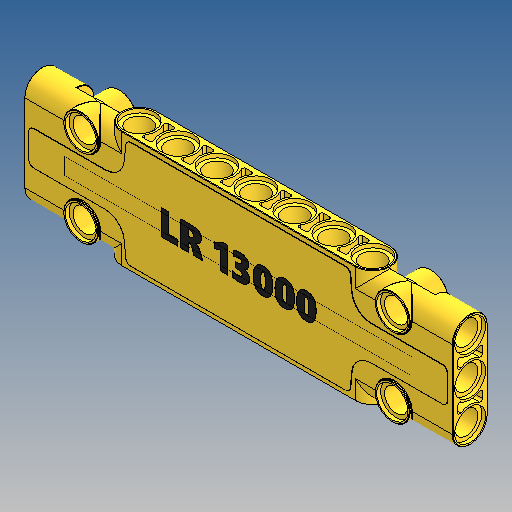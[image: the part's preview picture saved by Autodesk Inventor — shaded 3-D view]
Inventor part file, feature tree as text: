
AUTODESK INVENTOR PART (.ipt)
format: ipt  version: 2025 (Build 290162010, 162A)  size: 1,306,624 bytes
history: native  units: in
note: dims shown in document units (in); Inventor stores cm internally (conversion verified against a paired STEP export)
features: extrude x18, sketch x13, mirror x5, plane x1, fillet x1
ambient origin geometry x8: Origin, YZ Plane, XZ Plane, XY Plane, X Axis, Y Axis, Z Axis, Center Point
bodies: Solid1 (feature_tree)
feature tree (38):
  extrude  "Extrusion1"  Depth=0.189in
  sketch  "Sketch3"  dims[d6=0.189in d7=0.252in]
  extrude  "Extrusion2"  Depth=0.0315in
  extrude  "Extrusion3"  TaperAngle=0.0deg  [1 undecoded]
  extrude  "Extrusion4"  Depth=0.252in
  plane  "Work Plane1"
  extrude  "Extrusion5"  Depth=0.7874in
  sketch  "Sketch5"  dims[d12=0.3937in d14=0.3937in d16=0.2835in]
  extrude  "Extrusion6"  Depth=0.2835in
  extrude  "Extrusion7"  Depth=0.0315in
  extrude  "Extrusion10"  Depth=0.2205in TaperAngle=0.0deg
  extrude  "Extrusion8"  Depth=0.189in
  extrude  "Extrusion9"  Depth=0.0315in TaperAngle=0.0deg
  mirror  "Mirror1"
  mirror  "Mirror2"
  sketch  "Sketch8"  dims[d22=-0.1417in d23=0.189in]
  extrude  "Extrusion11"  Depth=0.189in
  extrude  "Extrusion12"  Depth=0.2677in
  extrude  "Extrusion13"  Depth=0.2677in TaperAngle=0.0deg
  sketch  "Sketch9"  dims[d24=0.2835in d25=0.0315in d26=0.0in]
  extrude  "Extrusion14"  Depth=0.252in
  extrude  "Extrusion16"  Depth=0.0315in
  mirror  "Mirror3"
  extrude  "Extrusion15"  TaperAngle=0.0deg  [1 undecoded]
  fillet  "Fillet1"  Radius=0.252in
  extrude  "Extrusion17"  Depth=0.0315in
  mirror  "Spiegeln4"
  mirror  "Spiegeln5"
  extrude  "Extrusion18"  TaperAngle=0.0deg  [1 undecoded]
  sketch  "Sketch2"  dims[d2=0.2835in d3=0.0315in]
  sketch  "Skizze - Rechteckige Anordnung1"  dims[d0=0.315in d1=0.189in]
  sketch  "Sketch4"  dims[d8=45.0deg d9=0.7874in d11=0.315in]
  sketch  "Sketch6"  dims[d17=0.0in d18=0.0315in]
  sketch  "Sketch7"  dims[d19=0.0in d20=0.2205in d21=0.0in]
  sketch  "Sketch10"  dims[d27=0.2835in d28=0.189in]
  sketch  "Skizze - Rechteckige Anordnung2"  dims[d4=3.4646in d5=0.0in]
  sketch  "Skizze11"  dims[d29=1.2598in d30=0.2677in d31=0.0472in]
  sketch  "Skizze12"  dims[d32=0.0in d33=0.0in d34=0.2677in d35=0.0in d36=0.252in d37=0.0315in d38=0.0in d39=0.252in d40=0.0315in d41=0.0in d42=0.0315in d43=0.2205in d44=0.0in d45=0.2835in d46=1.8898in d47=0.189in d48=0.1417in d49=0.1417in d50=0.0in d51=0.0in d52=0.1417in d53=0.0in d54=0.315in d55=0.0in d56=0.252in d57=0.0315in d58=0.0in d59=2.8031in d60=0.126in d62=0.0079in d63=0.0in d64=45.0deg d65=2.3622in d67=0.315in d68=0.3937in d70=0.3937in d72=0.2205in d73=0.0in d74=0.0039in d75=0.0157in d76=0.6528in d77=0.0394in d78=0.1378in d79=0.0394in d80=0.0394in d81=0.0394in d82=0.8268in d83=0.1575in d84=0.0039in d85=0.0in d86=0.0004in d87=0.0in]
note: 3 required parameter values undecoded (feature->parameter linkage not recoverable at this tier; creation-order binding heuristic only, values carry confidence <= 0.55)
